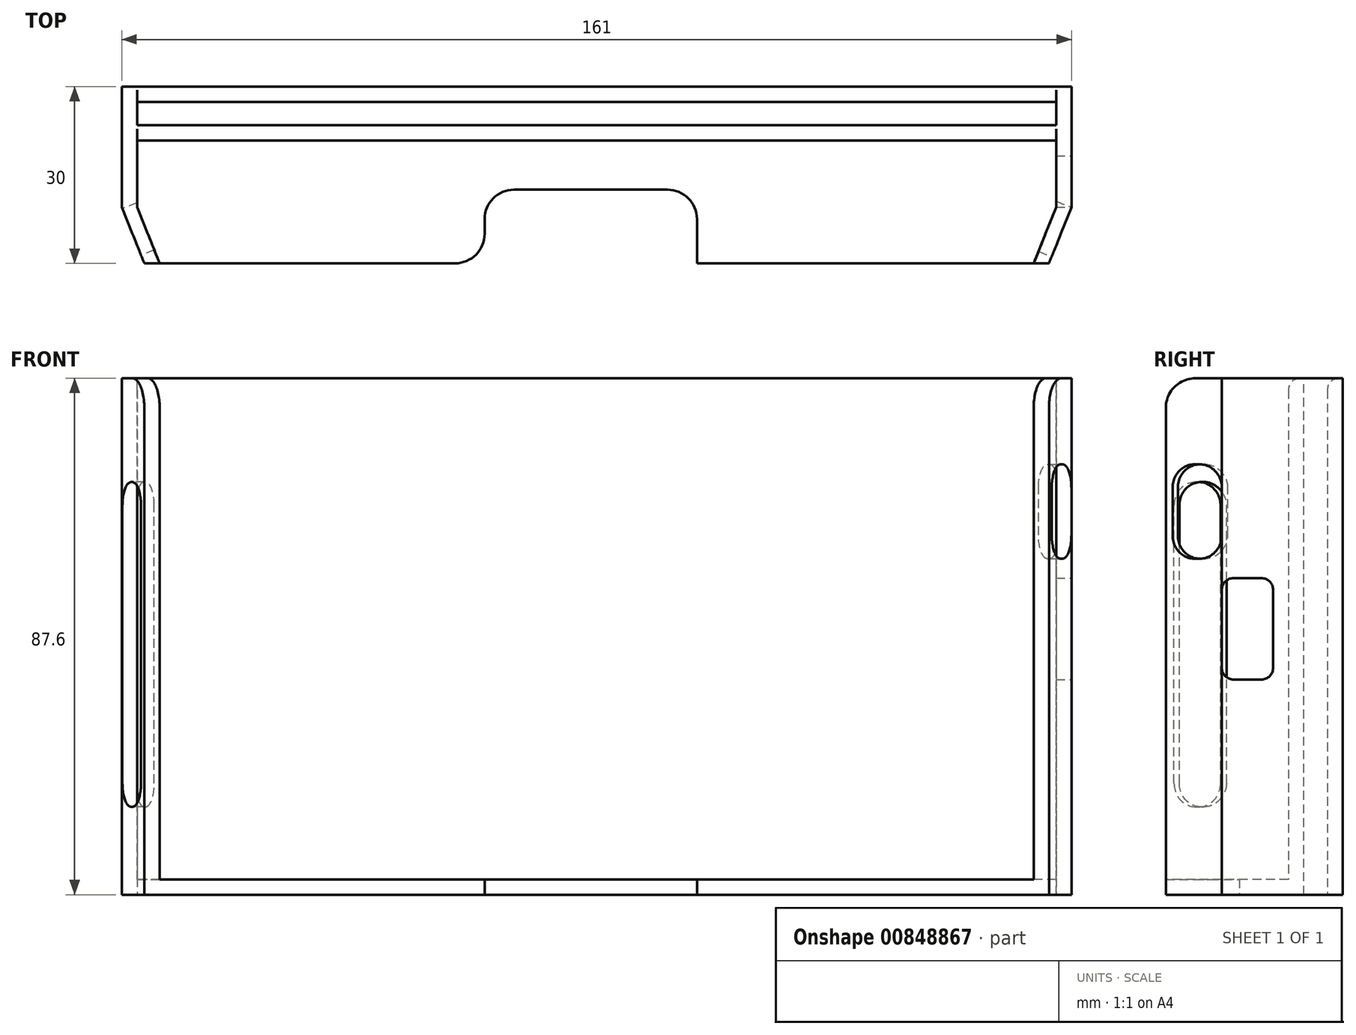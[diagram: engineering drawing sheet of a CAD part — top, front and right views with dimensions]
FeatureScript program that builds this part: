
annotation { "Feature Type Name" : "Feature", "Feature Type Description" : "" }
export const myFeature = defineFeature(function(context is Context, id is Id, definition is map)
    precondition{}
    {
        {
            var Q0;
            Q0=qCreatedBy(makeId("Front.planeOp"),FACE);
            var sketch = newSketch(context, id + "F0", { "sketchPlane" : qUnion([Q0])});
            skLineSegment(sketch, "E0.bottom", {"start": v(77.9, 42.5) * mm, "end": v(-77.9, 42.5) * mm});
            skLineSegment(sketch, "E0.top", {"start": v(77.9, -42.5) * mm, "end": v(-77.9, -42.5) * mm});
            skLineSegment(sketch, "E0.left", {"start": v(77.9, 42.5) * mm, "end": v(77.9, -42.5) * mm});
            skLineSegment(sketch, "E0.right", {"start": v(-77.9, 42.5) * mm, "end": v(-77.9, -42.5) * mm});
            skPoint(sketch, "E0.middle", {"position": v(0, 0) * mm});
            skSolve(sketch);
        }
        {
            var Q0;
            Q0=makeQuery(id+"F0.imprint","IMPRINT",FACE,{"disambiguationData":[TD([[makeQuery(id+"F0.imprint","IMPRINT",EDGE,{"derivedFrom":sQuery(id+"F0.wireOp",EDGE,"E0.bottom")}),1.0]])]});
            extrude(context, id + "F1", {"entities" : qUnion([Q0]), "depth" : 2.6 * mm, "offsetDistance" : 25 * mm});
        }
        {
            var Q0;
            Q0=makeQuery(id+"F1.opExtrude","SWEPT_FACE",FACE,{"disambiguationData":[OSD([sQuery(id+"F0.wireOp",EDGE,"E0.bottom")])]});
            var sketch = newSketch(context, id + "F2", { "sketchPlane" : qUnion([Q0])});
            skLineSegment(sketch, "E1", {"start": v(-77.9, -2.6) * mm, "end": v(-77.9, -13.9) * mm});
            skLineSegment(sketch, "E2", {"start": v(-77.9, -13.9) * mm, "end": v(-80.5, -13.9) * mm});
            skLineSegment(sketch, "E3", {"start": v(-80.5, -13.9) * mm, "end": v(-80.5, 0) * mm});
            skLineSegment(sketch, "E4", {"start": v(-80.5, 0) * mm, "end": v(-77.9, 0) * mm});
            skLineSegment(sketch, "E5", {"start": v(-77.9, -13.9) * mm, "end": v(-77.9, -23.4) * mm, "construction": true});
            skLineSegment(sketch, "E6", {"start": v(-77.9, -23.4) * mm, "end": v(-74.1, -23.4) * mm, "construction": true});
            skLineSegment(sketch, "E7", {"start": v(-77.9, -13.9) * mm, "end": v(-74.1, -23.4) * mm});
            skLineSegment(sketch, "E8", {"start": v(-74.1, -23.4) * mm, "end": v(-76.7, -23.4) * mm});
            skLineSegment(sketch, "E9", {"start": v(-76.7, -23.4) * mm, "end": v(-80.5, -13.9) * mm});
            skLineSegment(sketch, "E10.MirrorCS", {"start": v(77.9, -2.6) * mm, "end": v(77.9, -13.9) * mm});
            skLineSegment(sketch, "E11.MirrorCS", {"start": v(80.5, -13.9) * mm, "end": v(80.5, 0) * mm});
            skLineSegment(sketch, "E12.MirrorCS", {"start": v(76.7, -23.4) * mm, "end": v(80.5, -13.9) * mm});
            skLineSegment(sketch, "E13.MirrorCS", {"start": v(77.9, -13.9) * mm, "end": v(74.1, -23.4) * mm});
            skLineSegment(sketch, "E14.MirrorCS", {"start": v(80.5, 0) * mm, "end": v(77.9, 0) * mm});
            skLineSegment(sketch, "E15", {"start": v(74.1, -23.4) * mm, "end": v(76.7, -23.4) * mm});
            skSolve(sketch);
        }
        {
            var Q0;
            Q0=makeQuery(id+"F2.imprint","IMPRINT",FACE,{"disambiguationData":[TD([[makeQuery(id+"F2.imprint","IMPRINT",EDGE,{"derivedFrom":sQuery(id+"F2.wireOp",EDGE,"E1")}),-1.0]])]});
            var Q1;
            Q1=makeQuery(id+"F2.imprint","IMPRINT",FACE,{"disambiguationData":[TD([[makeQuery(id+"F2.imprint","IMPRINT",EDGE,{"derivedFrom":sQuery(id+"F2.wireOp",EDGE,"E2")}),1.0]])]});
            var Q2;
            Q2=makeQuery(id+"F2.imprint","IMPRINT",FACE,{"disambiguationData":[TD([[makeQuery(id+"F2.imprint","IMPRINT",EDGE,{"derivedFrom":sQuery(id+"F2.wireOp",EDGE,"E10.MirrorCS")}),1.0]])]});
            extrude(context, id + "F3", {"entities" : qUnion([Q0, Q1, Q2]), "operationType" : NewBodyOperationType.ADD, "oppositeDirection" : true, "depth" : 85 * mm, "offsetDistance" : 25 * mm});
        }
        {
            var Q0;
            {var subQ0=sQuery(id+"F0.wireOp",EDGE,"E0.bottom");Q0=makeQuery(id+"F3.boolean.opBoolean","MERGE",FACE,{"derivedFrom":[makeQuery(id+"F1.opExtrude","SWEPT_FACE",FACE,{"disambiguationData":[OSD([sQuery(id+"F0.wireOp",EDGE,"E0.top")])]}),makeQuery(id+"F3.opExtrude","CAP_FACE",FACE,{"disambiguationData":[OSD([subQ0,sQuery(id+"F0.wireOp",EDGE,"E0.right"),sQuery(id+"F2.wireOp",EDGE,"E1"),sQuery(id+"F2.wireOp",EDGE,"E3"),sQuery(id+"F2.wireOp",EDGE,"E4"),sQuery(id+"F2.wireOp",EDGE,"E7"),sQuery(id+"F2.wireOp",EDGE,"E8"),sQuery(id+"F2.wireOp",EDGE,"E9")])],"isStart":false}),makeQuery(id+"F3.opExtrude","CAP_FACE",FACE,{"disambiguationData":[OSD([subQ0,sQuery(id+"F0.wireOp",EDGE,"E0.left"),sQuery(id+"F2.wireOp",EDGE,"E10.MirrorCS"),sQuery(id+"F2.wireOp",EDGE,"E11.MirrorCS"),sQuery(id+"F2.wireOp",EDGE,"E12.MirrorCS"),sQuery(id+"F2.wireOp",EDGE,"E13.MirrorCS"),sQuery(id+"F2.wireOp",EDGE,"E14.MirrorCS"),sQuery(id+"F2.wireOp",EDGE,"E15")])],"isStart":false})]});}
            var sketch = newSketch(context, id + "F4", { "sketchPlane" : qUnion([Q0])});
            skLineSegment(sketch, "E16", {"start": v(-74.1, 23.4) * mm, "end": v(74.1, 23.4) * mm});
            skLineSegment(sketch, "E17", {"start": v(74.1, 23.4) * mm, "end": v(76.7, 23.4) * mm});
            skLineSegment(sketch, "E18", {"start": v(76.7, 23.4) * mm, "end": v(80.5, 13.9) * mm});
            skLineSegment(sketch, "E19", {"start": v(80.5, 13.9) * mm, "end": v(80.5, 0) * mm});
            skLineSegment(sketch, "E20", {"start": v(80.5, 0) * mm, "end": v(-80.5, 0) * mm});
            skLineSegment(sketch, "E21", {"start": v(-80.5, 0) * mm, "end": v(-80.5, 13.9) * mm});
            skLineSegment(sketch, "E22", {"start": v(-80.5, 13.9) * mm, "end": v(-76.7, 23.4) * mm});
            skLineSegment(sketch, "E23", {"start": v(-76.7, 23.4) * mm, "end": v(-74.1, 23.4) * mm});
            skSolve(sketch);
        }
        {
            var Q0;
            Q0=makeQuery(id+"F4.imprint","IMPRINT",FACE,{"disambiguationData":[TD([[makeQuery(id+"F4.imprint","IMPRINT",EDGE,{"derivedFrom":sQuery(id+"F4.wireOp",EDGE,"E16")}),-1.0]])]});
            var Q1;
            Q1=makeQuery(id+"F4.imprint","IMPRINT",FACE,{"disambiguationData":[TD([[makeQuery(id+"F4.imprint","IMPRINT",EDGE,{"derivedFrom":sQuery(id+"F4.wireOp",EDGE,"E17")}),-1.0]])]});
            extrude(context, id + "F5", {"entities" : qUnion([Q0, Q1]), "operationType" : NewBodyOperationType.ADD, "depth" : 2.6 * mm, "offsetDistance" : 25 * mm});
        }
        {
            var Q0;
            Q0=makeQuery(id+"F5.boolean.opBoolean","MERGE",FACE,{"derivedFrom":[makeQuery(id+"F3.opExtrude","SWEPT_FACE",FACE,{"disambiguationData":[OSD([sQuery(id+"F2.wireOp",EDGE,"E11.MirrorCS")])]}),makeQuery(id+"F5.opExtrude","SWEPT_FACE",FACE,{"disambiguationData":[OSD([sQuery(id+"F4.wireOp",EDGE,"E19")])]})]});
            var sketch = newSketch(context, id + "F6", { "sketchPlane" : qUnion([Q0])});
            skLineSegment(sketch, "E24.bottom", {"start": v(-13.9, 8.6) * mm, "end": v(-5.2, 8.6) * mm});
            skLineSegment(sketch, "E24.top", {"start": v(-13.9, -8.6) * mm, "end": v(-5.2, -8.6) * mm});
            skLineSegment(sketch, "E24.left", {"start": v(-13.9, 8.6) * mm, "end": v(-13.9, -8.6) * mm});
            skLineSegment(sketch, "E24.right", {"start": v(-5.2, 8.6) * mm, "end": v(-5.2, -8.6) * mm});
            skSolve(sketch);
        }
        {
            var Q0;
            Q0=makeQuery(id+"F6.imprint","IMPRINT",FACE,{"disambiguationData":[TD([[makeQuery(id+"F6.imprint","IMPRINT",EDGE,{"derivedFrom":sQuery(id+"F6.wireOp",EDGE,"E24.bottom")}),-1.0]])]});
            extrude(context, id + "F7", {"entities" : qUnion([Q0]), "operationType" : NewBodyOperationType.REMOVE, "oppositeDirection" : true, "depth" : 25 * mm, "offsetDistance" : 25 * mm});
        }
        {
            var Q0;
            Q0=makeQuery(id+"F5.boolean.opBoolean","MERGE",FACE,{"derivedFrom":[makeQuery(id+"F3.opExtrude","SWEPT_FACE",FACE,{"disambiguationData":[OSD([sQuery(id+"F2.wireOp",EDGE,"E12.MirrorCS")])]}),makeQuery(id+"F5.opExtrude","SWEPT_FACE",FACE,{"disambiguationData":[OSD([sQuery(id+"F4.wireOp",EDGE,"E18")])]})]});
            var sketch = newSketch(context, id + "F8", { "sketchPlane" : qUnion([Q0])});
            skLineSegment(sketch, "E25.bottom", {"start": v(17, 27.9) * mm, "end": v(8, 27.9) * mm});
            skLineSegment(sketch, "E25.top", {"start": v(17, 11.9) * mm, "end": v(8, 11.9) * mm});
            skLineSegment(sketch, "E25.left", {"start": v(17, 27.9) * mm, "end": v(17, 11.9) * mm});
            skLineSegment(sketch, "E25.right", {"start": v(8, 27.9) * mm, "end": v(8, 11.9) * mm});
            skSolve(sketch);
        }
        {
            var Q0;
            Q0=makeQuery(id+"F8.imprint","IMPRINT",FACE,{"disambiguationData":[TD([[makeQuery(id+"F8.imprint","IMPRINT",EDGE,{"derivedFrom":sQuery(id+"F8.wireOp",EDGE,"E25.bottom")}),1.0]])]});
            extrude(context, id + "F9", {"entities" : qUnion([Q0]), "operationType" : NewBodyOperationType.REMOVE, "oppositeDirection" : true, "depth" : 25 * mm, "offsetDistance" : 25 * mm});
        }
        {
            var Q0;
            Q0=makeQuery(id+"F5.boolean.opBoolean","MERGE",FACE,{"derivedFrom":[makeQuery(id+"F3.opExtrude","SWEPT_FACE",FACE,{"disambiguationData":[OSD([sQuery(id+"F2.wireOp",EDGE,"E9")])]}),makeQuery(id+"F5.opExtrude","SWEPT_FACE",FACE,{"disambiguationData":[OSD([sQuery(id+"F4.wireOp",EDGE,"E22")])]})]});
            var sketch = newSketch(context, id + "F10", { "sketchPlane" : qUnion([Q0])});
            skLineSegment(sketch, "E26.bottom", {"start": v(-8.26, -30.2) * mm, "end": v(-16.76, -30.2) * mm});
            skLineSegment(sketch, "E26.top", {"start": v(-8.26, 24.9) * mm, "end": v(-16.76, 24.9) * mm});
            skLineSegment(sketch, "E26.left", {"start": v(-8.26, -30.2) * mm, "end": v(-8.26, 24.9) * mm});
            skLineSegment(sketch, "E26.right", {"start": v(-16.76, -30.2) * mm, "end": v(-16.76, 24.9) * mm});
            skSolve(sketch);
        }
        {
            var Q0;
            Q0=makeQuery(id+"F10.imprint","IMPRINT",FACE,{"disambiguationData":[TD([[makeQuery(id+"F10.imprint","IMPRINT",EDGE,{"derivedFrom":sQuery(id+"F10.wireOp",EDGE,"E26.bottom")}),-1.0]])]});
            extrude(context, id + "F11", {"entities" : qUnion([Q0]), "operationType" : NewBodyOperationType.REMOVE, "oppositeDirection" : true, "depth" : 25 * mm, "offsetDistance" : 25 * mm});
        }
        {
            var Q0;
            Q0=makeQuery(id+"F5.boolean.opBoolean","MERGE",FACE,{"derivedFrom":[makeQuery(id+"F3.opExtrude","SWEPT_FACE",FACE,{"disambiguationData":[OSD([sQuery(id+"F2.wireOp",EDGE,"E3")])]}),makeQuery(id+"F5.opExtrude","SWEPT_FACE",FACE,{"disambiguationData":[OSD([sQuery(id+"F4.wireOp",EDGE,"E21")])]})]});
            var sketch = newSketch(context, id + "F12", { "sketchPlane" : qUnion([Q0])});
            skLineSegment(sketch, "E27.bottom", {"start": v(0, 42.5) * mm, "end": v(-6.6, 42.5) * mm});
            skLineSegment(sketch, "E27.top", {"start": v(0, -45.1) * mm, "end": v(-6.6, -45.1) * mm});
            skLineSegment(sketch, "E27.left", {"start": v(0, 42.5) * mm, "end": v(0, -45.1) * mm});
            skLineSegment(sketch, "E27.right", {"start": v(-6.6, 42.5) * mm, "end": v(-6.6, -45.1) * mm});
            skSolve(sketch);
        }
        {
            var Q0;
            Q0 = qSketchRegion(id + "F12", true);
            extrude(context, id + "F13", {"entities" : qUnion([Q0]), "oppositeDirection" : true, "depth" : 2.6 * mm, "offsetDistance" : 25 * mm});
        }
        {
            var Q0;
            Q0=makeQuery(id+"F5.boolean.opBoolean","MERGE",FACE,{"derivedFrom":[makeQuery(id+"F3.opExtrude","SWEPT_FACE",FACE,{"disambiguationData":[OSD([sQuery(id+"F2.wireOp",EDGE,"E11.MirrorCS")])]}),makeQuery(id+"F5.opExtrude","SWEPT_FACE",FACE,{"disambiguationData":[OSD([sQuery(id+"F4.wireOp",EDGE,"E19")])]})]});
            var sketch = newSketch(context, id + "F14", { "sketchPlane" : qUnion([Q0])});
            skLineSegment(sketch, "E28.bottom", {"start": v(0, 42.5) * mm, "end": v(6.6, 42.5) * mm});
            skLineSegment(sketch, "E28.top", {"start": v(0, -45.1) * mm, "end": v(6.6, -45.1) * mm});
            skLineSegment(sketch, "E28.left", {"start": v(0, 42.5) * mm, "end": v(0, -45.1) * mm});
            skLineSegment(sketch, "E28.right", {"start": v(6.6, 42.5) * mm, "end": v(6.6, -45.1) * mm});
            skSolve(sketch);
        }
        {
            var Q0;
            Q0=makeQuery(id+"F14.imprint","IMPRINT",FACE,{"disambiguationData":[TD([[makeQuery(id+"F14.imprint","IMPRINT",EDGE,{"derivedFrom":sQuery(id+"F14.wireOp",EDGE,"E28.bottom")}),-1.0]])]});
            extrude(context, id + "F15", {"entities" : qUnion([Q0]), "operationType" : NewBodyOperationType.ADD, "oppositeDirection" : true, "depth" : 2.6 * mm, "offsetDistance" : 25 * mm});
        }
        {
            var Q0;
            Q0=makeQuery(id+"F15.opExtrude","SWEPT_FACE",FACE,{"disambiguationData":[OSD([sQuery(id+"F14.wireOp",EDGE,"E28.right")])]});
            var sketch = newSketch(context, id + "F16", { "sketchPlane" : qUnion([Q0])});
            skLineSegment(sketch, "E29.bottom", {"start": v(-77.9, 42.5) * mm, "end": v(77.9, 42.5) * mm});
            skLineSegment(sketch, "E29.top", {"start": v(-77.9, -45.1) * mm, "end": v(77.9, -45.1) * mm});
            skLineSegment(sketch, "E29.left", {"start": v(-77.9, 42.5) * mm, "end": v(-77.9, -45.1) * mm});
            skLineSegment(sketch, "E29.right", {"start": v(77.9, 42.5) * mm, "end": v(77.9, -45.1) * mm});
            skSolve(sketch);
        }
        {
            var Q0;
            Q0=makeQuery(id+"F16.imprint","IMPRINT",FACE,{"disambiguationData":[TD([[makeQuery(id+"F16.imprint","IMPRINT",EDGE,{"derivedFrom":sQuery(id+"F16.wireOp",EDGE,"E29.bottom")}),-1.0]])]});
            extrude(context, id + "F17", {"entities" : qUnion([Q0]), "oppositeDirection" : true, "depth" : 2.6 * mm, "offsetDistance" : 25 * mm});
        }
        {
            var Q0;
            Q0=makeQuery(id+"F17.opExtrude","SWEPT_BODY",BODY,{"disambiguationData":[OSD([sQuery(id+"F16.wireOp",EDGE,"E29.bottom"),sQuery(id+"F16.wireOp",EDGE,"E29.top"),sQuery(id+"F16.wireOp",EDGE,"E29.left"),sQuery(id+"F16.wireOp",EDGE,"E29.right")])]});
            var Q1;
            Q1=makeQuery(id+"F13.opExtrude","SWEPT_BODY",BODY,{"disambiguationData":[OSD([sQuery(id+"F12.wireOp",EDGE,"E27.bottom"),sQuery(id+"F12.wireOp",EDGE,"E27.top"),sQuery(id+"F12.wireOp",EDGE,"E27.left"),sQuery(id+"F12.wireOp",EDGE,"E27.right")])]});
            var Q2;
            Q2=makeQuery(id+"F1.opExtrude","SWEPT_BODY",BODY,{"disambiguationData":[OSD([sQuery(id+"F0.wireOp",EDGE,"E0.bottom"),sQuery(id+"F0.wireOp",EDGE,"E0.top"),sQuery(id+"F0.wireOp",EDGE,"E0.left"),sQuery(id+"F0.wireOp",EDGE,"E0.right")])]});
            booleanBodies(context, id + "F18", {"operationType" : BooleanOperationType.UNION, "tools" : qUnion([Q0, Q1, Q2])});
        }
        {
            var Q0;
            Q0=makeQuery(id+"F18.opBoolean","MERGE",FACE,{"derivedFrom":[makeQuery(id+"F13.opExtrude","SWEPT_FACE",FACE,{"disambiguationData":[OSD([sQuery(id+"F12.wireOp",EDGE,"E27.top")])]}),makeQuery(id+"F15.boolean.opBoolean","MERGE",FACE,{"derivedFrom":[makeQuery(id+"F5.opExtrude","CAP_FACE",FACE,{"disambiguationData":[OSD([sQuery(id+"F4.wireOp",EDGE,"E16"),sQuery(id+"F4.wireOp",EDGE,"E17"),sQuery(id+"F4.wireOp",EDGE,"E18"),sQuery(id+"F4.wireOp",EDGE,"E19"),sQuery(id+"F4.wireOp",EDGE,"E20"),sQuery(id+"F4.wireOp",EDGE,"E21"),sQuery(id+"F4.wireOp",EDGE,"E22"),sQuery(id+"F4.wireOp",EDGE,"E23")])],"isStart":false}),makeQuery(id+"F15.opExtrude","SWEPT_FACE",FACE,{"disambiguationData":[OSD([sQuery(id+"F14.wireOp",EDGE,"E28.top")])]})]}),makeQuery(id+"F17.opExtrude","SWEPT_FACE",FACE,{"disambiguationData":[OSD([sQuery(id+"F16.wireOp",EDGE,"E29.top")])]})]});
            var sketch = newSketch(context, id + "F19", { "sketchPlane" : qUnion([Q0])});
            skLineSegment(sketch, "E30.bottom", {"start": v(-19, 23.4) * mm, "end": v(17, 23.4) * mm});
            skLineSegment(sketch, "E30.top", {"start": v(-19, 10.9) * mm, "end": v(17, 10.9) * mm});
            skLineSegment(sketch, "E30.left", {"start": v(-19, 23.4) * mm, "end": v(-19, 10.9) * mm});
            skLineSegment(sketch, "E30.right", {"start": v(17, 23.4) * mm, "end": v(17, 10.9) * mm});
            skSolve(sketch);
        }
        {
            var Q0;
            Q0=makeQuery(id+"F19.imprint","IMPRINT",FACE,{"disambiguationData":[TD([[makeQuery(id+"F19.imprint","IMPRINT",EDGE,{"derivedFrom":sQuery(id+"F19.wireOp",EDGE,"E30.bottom")}),-1.0]])]});
            extrude(context, id + "F20", {"entities" : qUnion([Q0]), "operationType" : NewBodyOperationType.REMOVE, "oppositeDirection" : true, "depth" : 25 * mm, "offsetDistance" : 25 * mm});
        }
        {
            var Q0;
            Q0=makeQuery(id+"F11.boolean.opBoolean","COPY",EDGE,{"derivedFrom":makeQuery(id+"F11.opExtrude","SWEPT_EDGE",EDGE,{"disambiguationData":[OSD([sQuery(id+"F10.wireOp",EDGE,"E26.bottom"),sQuery(id+"F10.wireOp",EDGE,"E26.right")])]})});
            var Q1;
            Q1=makeQuery(id+"F11.boolean.opBoolean","COPY",EDGE,{"derivedFrom":makeQuery(id+"F11.opExtrude","SWEPT_EDGE",EDGE,{"disambiguationData":[OSD([sQuery(id+"F10.wireOp",EDGE,"E26.bottom"),sQuery(id+"F10.wireOp",EDGE,"E26.left")])]})});
            var Q2;
            Q2=makeQuery(id+"F11.boolean.opBoolean","COPY",EDGE,{"derivedFrom":makeQuery(id+"F11.opExtrude","SWEPT_EDGE",EDGE,{"disambiguationData":[OSD([sQuery(id+"F10.wireOp",EDGE,"E26.top"),sQuery(id+"F10.wireOp",EDGE,"E26.left")])]})});
            var Q3;
            Q3=makeQuery(id+"F11.boolean.opBoolean","COPY",EDGE,{"derivedFrom":makeQuery(id+"F11.opExtrude","SWEPT_EDGE",EDGE,{"disambiguationData":[OSD([sQuery(id+"F10.wireOp",EDGE,"E26.top"),sQuery(id+"F10.wireOp",EDGE,"E26.right")])]})});
            fillet(context, id + "F21", {"entities" : qUnion([Q0, Q1, Q2, Q3]), "radius" : 4 * mm, "tangentPropagation" : true, "allowEdgeOverflow" : false});
        }
        {
            var Q0;
            Q0=makeQuery(id+"F9.boolean.opBoolean","COPY",EDGE,{"derivedFrom":makeQuery(id+"F9.opExtrude","SWEPT_EDGE",EDGE,{"disambiguationData":[OSD([sQuery(id+"F8.wireOp",EDGE,"E25.top"),sQuery(id+"F8.wireOp",EDGE,"E25.right")])]})});
            var Q1;
            Q1=makeQuery(id+"F9.boolean.opBoolean","COPY",EDGE,{"derivedFrom":makeQuery(id+"F9.opExtrude","SWEPT_EDGE",EDGE,{"disambiguationData":[OSD([sQuery(id+"F2.wireOp",EDGE,"E11.MirrorCS"),sQuery(id+"F2.wireOp",EDGE,"E12.MirrorCS"),sQuery(id+"F4.wireOp",EDGE,"E18"),sQuery(id+"F4.wireOp",EDGE,"E19"),sQuery(id+"F8.wireOp",EDGE,"E25.top"),sQuery(id+"F8.wireOp",EDGE,"E25.left")])]})});
            var Q2;
            Q2=makeQuery(id+"F9.boolean.opBoolean","COPY",EDGE,{"derivedFrom":makeQuery(id+"F9.opExtrude","SWEPT_EDGE",EDGE,{"disambiguationData":[OSD([sQuery(id+"F8.wireOp",EDGE,"E25.bottom"),sQuery(id+"F8.wireOp",EDGE,"E25.right")])]})});
            var Q3;
            Q3=makeQuery(id+"F9.boolean.opBoolean","COPY",EDGE,{"derivedFrom":makeQuery(id+"F9.opExtrude","SWEPT_EDGE",EDGE,{"disambiguationData":[OSD([sQuery(id+"F2.wireOp",EDGE,"E11.MirrorCS"),sQuery(id+"F2.wireOp",EDGE,"E12.MirrorCS"),sQuery(id+"F4.wireOp",EDGE,"E18"),sQuery(id+"F4.wireOp",EDGE,"E19"),sQuery(id+"F8.wireOp",EDGE,"E25.bottom"),sQuery(id+"F8.wireOp",EDGE,"E25.left")])]})});
            fillet(context, id + "F22", {"entities" : qUnion([Q0, Q1, Q2, Q3]), "radius" : 4 * mm, "tangentPropagation" : true, "allowEdgeOverflow" : false});
        }
        {
            var Q0;
            Q0=makeQuery(id+"F7.boolean.opBoolean","COPY",EDGE,{"derivedFrom":makeQuery(id+"F7.opExtrude","SWEPT_EDGE",EDGE,{"disambiguationData":[OSD([sQuery(id+"F2.wireOp",EDGE,"E11.MirrorCS"),sQuery(id+"F2.wireOp",EDGE,"E12.MirrorCS"),sQuery(id+"F4.wireOp",EDGE,"E18"),sQuery(id+"F4.wireOp",EDGE,"E19"),sQuery(id+"F6.wireOp",EDGE,"E24.bottom"),sQuery(id+"F6.wireOp",EDGE,"E24.left")])]})});
            var Q1;
            Q1=makeQuery(id+"F7.boolean.opBoolean","COPY",EDGE,{"derivedFrom":makeQuery(id+"F7.opExtrude","SWEPT_EDGE",EDGE,{"disambiguationData":[OSD([sQuery(id+"F6.wireOp",EDGE,"E24.bottom"),sQuery(id+"F6.wireOp",EDGE,"E24.right")])]})});
            var Q2;
            Q2=makeQuery(id+"F7.boolean.opBoolean","COPY",EDGE,{"derivedFrom":makeQuery(id+"F7.opExtrude","SWEPT_EDGE",EDGE,{"disambiguationData":[OSD([sQuery(id+"F6.wireOp",EDGE,"E24.top"),sQuery(id+"F6.wireOp",EDGE,"E24.right")])]})});
            var Q3;
            Q3=makeQuery(id+"F7.boolean.opBoolean","COPY",EDGE,{"derivedFrom":makeQuery(id+"F7.opExtrude","SWEPT_EDGE",EDGE,{"disambiguationData":[OSD([sQuery(id+"F2.wireOp",EDGE,"E11.MirrorCS"),sQuery(id+"F2.wireOp",EDGE,"E12.MirrorCS"),sQuery(id+"F4.wireOp",EDGE,"E18"),sQuery(id+"F4.wireOp",EDGE,"E19"),sQuery(id+"F6.wireOp",EDGE,"E24.top"),sQuery(id+"F6.wireOp",EDGE,"E24.left")])]})});
            fillet(context, id + "F23", {"entities" : qUnion([Q0, Q1, Q2, Q3]), "radius" : 2 * mm, "tangentPropagation" : true, "allowEdgeOverflow" : false});
        }
        {
            var Q0;
            Q0=makeQuery(id+"F20.boolean.opBoolean","COPY",EDGE,{"derivedFrom":makeQuery(id+"F20.opExtrude","SWEPT_EDGE",EDGE,{"disambiguationData":[OSD([sQuery(id+"F19.wireOp",EDGE,"E30.top"),sQuery(id+"F19.wireOp",EDGE,"E30.right")])]})});
            var Q1;
            Q1=makeQuery(id+"F20.boolean.opBoolean","COPY",EDGE,{"derivedFrom":makeQuery(id+"F20.opExtrude","SWEPT_EDGE",EDGE,{"disambiguationData":[OSD([sQuery(id+"F19.wireOp",EDGE,"E30.top"),sQuery(id+"F19.wireOp",EDGE,"E30.left")])]})});
            var Q2;
            Q2=makeQuery(id+"F20.boolean.opBoolean","COPY",EDGE,{"derivedFrom":makeQuery(id+"F20.opExtrude","SWEPT_EDGE",EDGE,{"disambiguationData":[OSD([sQuery(id+"F4.wireOp",EDGE,"E16"),sQuery(id+"F4.wireOp",EDGE,"E17"),sQuery(id+"F4.wireOp",EDGE,"E23"),sQuery(id+"F19.wireOp",EDGE,"E30.bottom"),sQuery(id+"F19.wireOp",EDGE,"E30.right")])]})});
            var Q3;
            Q3=makeQuery(id+"F20.boolean.opBoolean","COPY",EDGE,{"derivedFrom":makeQuery(id+"F20.opExtrude","SWEPT_EDGE",EDGE,{"disambiguationData":[OSD([sQuery(id+"F4.wireOp",EDGE,"E16"),sQuery(id+"F4.wireOp",EDGE,"E17"),sQuery(id+"F4.wireOp",EDGE,"E23"),sQuery(id+"F19.wireOp",EDGE,"E30.bottom"),sQuery(id+"F19.wireOp",EDGE,"E30.left")])]})});
            fillet(context, id + "F24", {"entities" : qUnion([Q0, Q1, Q2, Q3]), "radius" : 5 * mm, "tangentPropagation" : true, "allowEdgeOverflow" : false});
        }
        {
            var Q0;
            Q0=makeQuery(id+"F1.opExtrude","CAP_EDGE",EDGE,{"disambiguationData":[OSD([sQuery(id+"F0.wireOp",EDGE,"E0.bottom")])],"isStart":false});
            var Q1;
            Q1=makeQuery(id+"F17.opExtrude","CAP_EDGE",EDGE,{"disambiguationData":[OSD([sQuery(id+"F16.wireOp",EDGE,"E29.bottom")])],"isStart":false});
            fillet(context, id + "F25", {"entities" : qUnion([Q0, Q1]), "radius" : 2 * mm, "tangentPropagation" : true, "allowEdgeOverflow" : false});
        }
        {
            var Q0;
            Q0=makeQuery(id+"F3.opExtrude","CAP_EDGE",EDGE,{"disambiguationData":[OSD([sQuery(id+"F2.wireOp",EDGE,"E8")])],"isStart":true});
            var Q1;
            Q1=makeQuery(id+"F3.opExtrude","CAP_EDGE",EDGE,{"disambiguationData":[OSD([sQuery(id+"F2.wireOp",EDGE,"E15")])],"isStart":true});
            fillet(context, id + "F26", {"entities" : qUnion([Q0, Q1]), "radius" : 5 * mm, "tangentPropagation" : true, "allowEdgeOverflow" : false});
        }
    });
